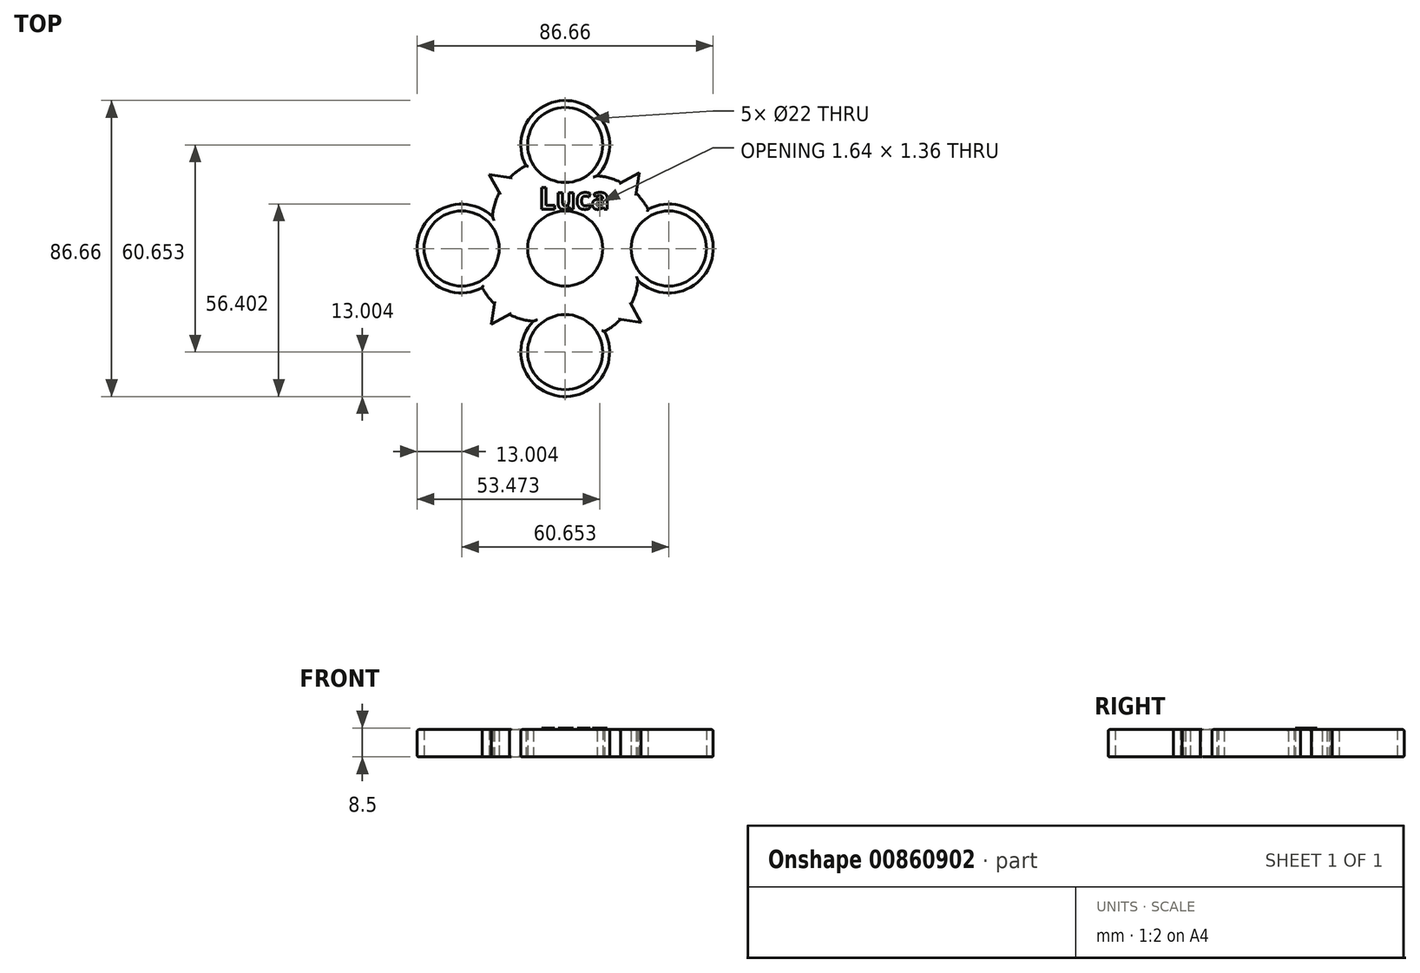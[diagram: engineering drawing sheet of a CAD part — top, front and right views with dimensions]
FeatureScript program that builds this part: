
annotation { "Feature Type Name" : "Feature", "Feature Type Description" : "" }
export const myFeature = defineFeature(function(context is Context, id is Id, definition is map)
    precondition{}
    {
        {
            var Q0;
            Q0=qCreatedBy(makeId("Top.planeOp"),FACE);
            var sketch = newSketch(context, id + "F0", { "sketchPlane" : qUnion([Q0])});
            skCircle(sketch, "E0", {"center": v(0, 0) * mm, "radius": 11 * mm});
            skCircle(sketch, "E1", {"center": v(0, 30.33) * mm, "radius": 11 * mm});
            skArc(sketch, "E2", {"start": v(9.35, 21.3) * mm, "mid": v(1.83, 43.2) * mm, "end": v(-11.5, 24.26) * mm});
            skCircle(sketch, "E3.1.0", {"center": v(-30.33, 0) * mm, "radius": 11 * mm});
            skArc(sketch, "E3.1.1", {"start": v(-21.3, 9.35) * mm, "mid": v(-43.2, 1.83) * mm, "end": v(-24.26, -11.5) * mm});
            skCircle(sketch, "E3.2.0", {"center": v(0, -30.33) * mm, "radius": 11 * mm});
            skArc(sketch, "E3.2.1", {"start": v(-9.35, -21.3) * mm, "mid": v(-1.83, -43.2) * mm, "end": v(11.5, -24.26) * mm});
            skCircle(sketch, "E3.3.0", {"center": v(30.33, 0) * mm, "radius": 11 * mm});
            skArc(sketch, "E3.3.1", {"start": v(21.3, -9.35) * mm, "mid": v(43.2, -1.83) * mm, "end": v(24.26, 11.5) * mm});
            skArc(sketch, "E4", {"start": v(-11.5, 24.26) * mm, "mid": v(-13.97, 22.69) * mm, "end": v(-16.16, 20.74) * mm});
            skArc(sketch, "E5.1.0", {"start": v(-24.26, -11.5) * mm, "mid": v(-22.69, -13.97) * mm, "end": v(-20.74, -16.16) * mm});
            skArc(sketch, "E5.2.0", {"start": v(11.5, -24.26) * mm, "mid": v(13.97, -22.69) * mm, "end": v(16.16, -20.74) * mm});
            skArc(sketch, "E5.3.0", {"start": v(24.26, 11.5) * mm, "mid": v(22.69, 13.97) * mm, "end": v(20.74, 16.16) * mm});
            skLineSegment(sketch, "E6", {"start": v(-19.3, 16.35) * mm, "end": v(-22.21, 21.66) * mm});
            skLineSegment(sketch, "E7", {"start": v(-22.21, 21.66) * mm, "end": v(-16.16, 20.74) * mm});
            skArc(sketch, "E8.trimOffspring", {"start": v(-19.3, 16.35) * mm, "mid": v(-20.64, 12.95) * mm, "end": v(-21.3, 9.35) * mm});
            skLineSegment(sketch, "E9.1.0", {"start": v(-16.35, -19.3) * mm, "end": v(-21.66, -22.21) * mm});
            skLineSegment(sketch, "E9.1.1", {"start": v(-21.66, -22.21) * mm, "end": v(-20.74, -16.16) * mm});
            skLineSegment(sketch, "E9.2.0", {"start": v(19.3, -16.35) * mm, "end": v(22.21, -21.66) * mm});
            skLineSegment(sketch, "E9.2.1", {"start": v(22.21, -21.66) * mm, "end": v(16.16, -20.74) * mm});
            skLineSegment(sketch, "E9.3.0", {"start": v(16.35, 19.3) * mm, "end": v(21.66, 22.21) * mm});
            skLineSegment(sketch, "E9.3.1", {"start": v(21.66, 22.21) * mm, "end": v(20.74, 16.16) * mm});
            skArc(sketch, "E10.trimOffspring", {"start": v(16.35, 19.3) * mm, "mid": v(12.95, 20.64) * mm, "end": v(9.35, 21.3) * mm});
            skArc(sketch, "E11.trimOffspring", {"start": v(19.3, -16.35) * mm, "mid": v(20.64, -12.95) * mm, "end": v(21.3, -9.35) * mm});
            skArc(sketch, "E12.trimOffspring", {"start": v(-16.35, -19.3) * mm, "mid": v(-12.95, -20.64) * mm, "end": v(-9.35, -21.3) * mm});
            skSolve(sketch);
        }
        {
            var Q0;
            Q0=makeQuery(id+"F0.imprint","IMPRINT",FACE,{"disambiguationData":[TD([[makeQuery(id+"F0.imprint","IMPRINT",EDGE,{"derivedFrom":sQuery(id+"F0.wireOp",EDGE,"E0")}),-1.0]])]});
            extrude(context, id + "F1", {"entities" : qUnion([Q0]), "depth" : 8 * mm, "offsetDistance" : 25 * mm});
        }
        {
            var Q0;
            Q0=makeQuery(id+"F1.opExtrude","CAP_EDGE",EDGE,{"disambiguationData":[OSD([sQuery(id+"F0.wireOp",EDGE,"E8.trimOffspring")])],"isStart":false});
            var Q1;
            Q1=makeQuery(id+"F1.opExtrude","CAP_EDGE",EDGE,{"disambiguationData":[OSD([sQuery(id+"F0.wireOp",EDGE,"E8.trimOffspring")])],"isStart":true});
            var Q2;
            Q2=makeQuery(id+"F1.opExtrude","CAP_EDGE",EDGE,{"disambiguationData":[OSD([sQuery(id+"F0.wireOp",EDGE,"E11.trimOffspring")])],"isStart":false});
            var Q3;
            Q3=makeQuery(id+"F1.opExtrude","CAP_EDGE",EDGE,{"disambiguationData":[OSD([sQuery(id+"F0.wireOp",EDGE,"E11.trimOffspring")])],"isStart":true});
            var Q4;
            Q4=makeQuery(id+"F1.opExtrude","CAP_EDGE",EDGE,{"disambiguationData":[OSD([sQuery(id+"F0.wireOp",EDGE,"E5.2.0")])],"isStart":true});
            var Q5;
            Q5=makeQuery(id+"F1.opExtrude","CAP_EDGE",EDGE,{"disambiguationData":[OSD([sQuery(id+"F0.wireOp",EDGE,"E5.2.0")])],"isStart":false});
            var Q6;
            Q6=makeQuery(id+"F1.opExtrude","CAP_EDGE",EDGE,{"disambiguationData":[OSD([sQuery(id+"F0.wireOp",EDGE,"E12.trimOffspring")])],"isStart":false});
            var Q7;
            Q7=makeQuery(id+"F1.opExtrude","CAP_EDGE",EDGE,{"disambiguationData":[OSD([sQuery(id+"F0.wireOp",EDGE,"E12.trimOffspring")])],"isStart":true});
            var Q8;
            Q8=makeQuery(id+"F1.opExtrude","CAP_EDGE",EDGE,{"disambiguationData":[OSD([sQuery(id+"F0.wireOp",EDGE,"E5.1.0")])],"isStart":true});
            var Q9;
            Q9=makeQuery(id+"F1.opExtrude","CAP_EDGE",EDGE,{"disambiguationData":[OSD([sQuery(id+"F0.wireOp",EDGE,"E5.1.0")])],"isStart":false});
            var Q10;
            Q10=makeQuery(id+"F1.opExtrude","CAP_EDGE",EDGE,{"disambiguationData":[OSD([sQuery(id+"F0.wireOp",EDGE,"E4")])],"isStart":false});
            var Q11;
            Q11=makeQuery(id+"F1.opExtrude","CAP_EDGE",EDGE,{"disambiguationData":[OSD([sQuery(id+"F0.wireOp",EDGE,"E4")])],"isStart":true});
            var Q12;
            Q12=makeQuery(id+"F1.opExtrude","CAP_EDGE",EDGE,{"disambiguationData":[OSD([sQuery(id+"F0.wireOp",EDGE,"E10.trimOffspring")])],"isStart":true});
            var Q13;
            Q13=makeQuery(id+"F1.opExtrude","CAP_EDGE",EDGE,{"disambiguationData":[OSD([sQuery(id+"F0.wireOp",EDGE,"E10.trimOffspring")])],"isStart":false});
            var Q14;
            Q14=makeQuery(id+"F1.opExtrude","CAP_EDGE",EDGE,{"disambiguationData":[OSD([sQuery(id+"F0.wireOp",EDGE,"E5.3.0")])],"isStart":false});
            var Q15;
            Q15=makeQuery(id+"F1.opExtrude","CAP_EDGE",EDGE,{"disambiguationData":[OSD([sQuery(id+"F0.wireOp",EDGE,"E5.3.0")])],"isStart":true});
            var Q16;
            Q16=makeQuery(id+"F1.opExtrude","CAP_EDGE",EDGE,{"disambiguationData":[OSD([sQuery(id+"F0.wireOp",EDGE,"E3.3.1")])],"isStart":false});
            var Q17;
            Q17=makeQuery(id+"F1.opExtrude","CAP_EDGE",EDGE,{"disambiguationData":[OSD([sQuery(id+"F0.wireOp",EDGE,"E3.3.1")])],"isStart":true});
            var Q18;
            Q18=makeQuery(id+"F1.opExtrude","CAP_EDGE",EDGE,{"disambiguationData":[OSD([sQuery(id+"F0.wireOp",EDGE,"E2")])],"isStart":true});
            var Q19;
            Q19=makeQuery(id+"F1.opExtrude","CAP_EDGE",EDGE,{"disambiguationData":[OSD([sQuery(id+"F0.wireOp",EDGE,"E2")])],"isStart":false});
            var Q20;
            Q20=makeQuery(id+"F1.opExtrude","CAP_EDGE",EDGE,{"disambiguationData":[OSD([sQuery(id+"F0.wireOp",EDGE,"E3.2.1")])],"isStart":false});
            var Q21;
            Q21=makeQuery(id+"F1.opExtrude","CAP_EDGE",EDGE,{"disambiguationData":[OSD([sQuery(id+"F0.wireOp",EDGE,"E3.2.1")])],"isStart":true});
            var Q22;
            Q22=makeQuery(id+"F1.opExtrude","CAP_EDGE",EDGE,{"disambiguationData":[OSD([sQuery(id+"F0.wireOp",EDGE,"E3.1.1")])],"isStart":false});
            var Q23;
            Q23=makeQuery(id+"F1.opExtrude","CAP_EDGE",EDGE,{"disambiguationData":[OSD([sQuery(id+"F0.wireOp",EDGE,"E3.1.1")])],"isStart":true});
            fillet(context, id + "F2", {"entities" : qUnion([Q0, Q1, Q2, Q3, Q4, Q5, Q6, Q7, Q8, Q9, Q10, Q11, Q12, Q13, Q14, Q15, Q16, Q17, Q18, Q19, Q20, Q21, Q22, Q23]), "radius" : 0.5 * mm, "tangentPropagation" : true, "allowEdgeOverflow" : false});
        }
        {
            var Q0;
            Q0=qCreatedBy(makeId("Top.planeOp"),FACE);
            cPlane(context, id + "F3", {"entities" : qUnion([Q0]), "cplaneType" : CPlaneType.OFFSET, "offset" : 8 * mm, "width" : 150 * mm, "height" : 150 * mm});
        }
        {
            var Q0;
            Q0=qCreatedBy(id+"F3.planeOp",FACE);
            var sketch = newSketch(context, id + "F4", { "sketchPlane" : qUnion([Q0])});
            skText(sketch, "E13", { "text": "Luca", "fontName": "OpenSans-Bold.ttf"});
            const initialGuessF4  = {"E13": [-0.00771, 0.01152, 1, 0, 0.00635]};
            skSetInitialGuess(sketch, initialGuessF4);
            skSolve(sketch);
        }
        {
            var Q0;
            Q0 = qSketchRegion(id + "F4", true);
            extrude(context, id + "F5", {"entities" : qUnion([Q0]), "depth" : 0.5 * mm, "offsetDistance" : 25 * mm});
        }
    });
